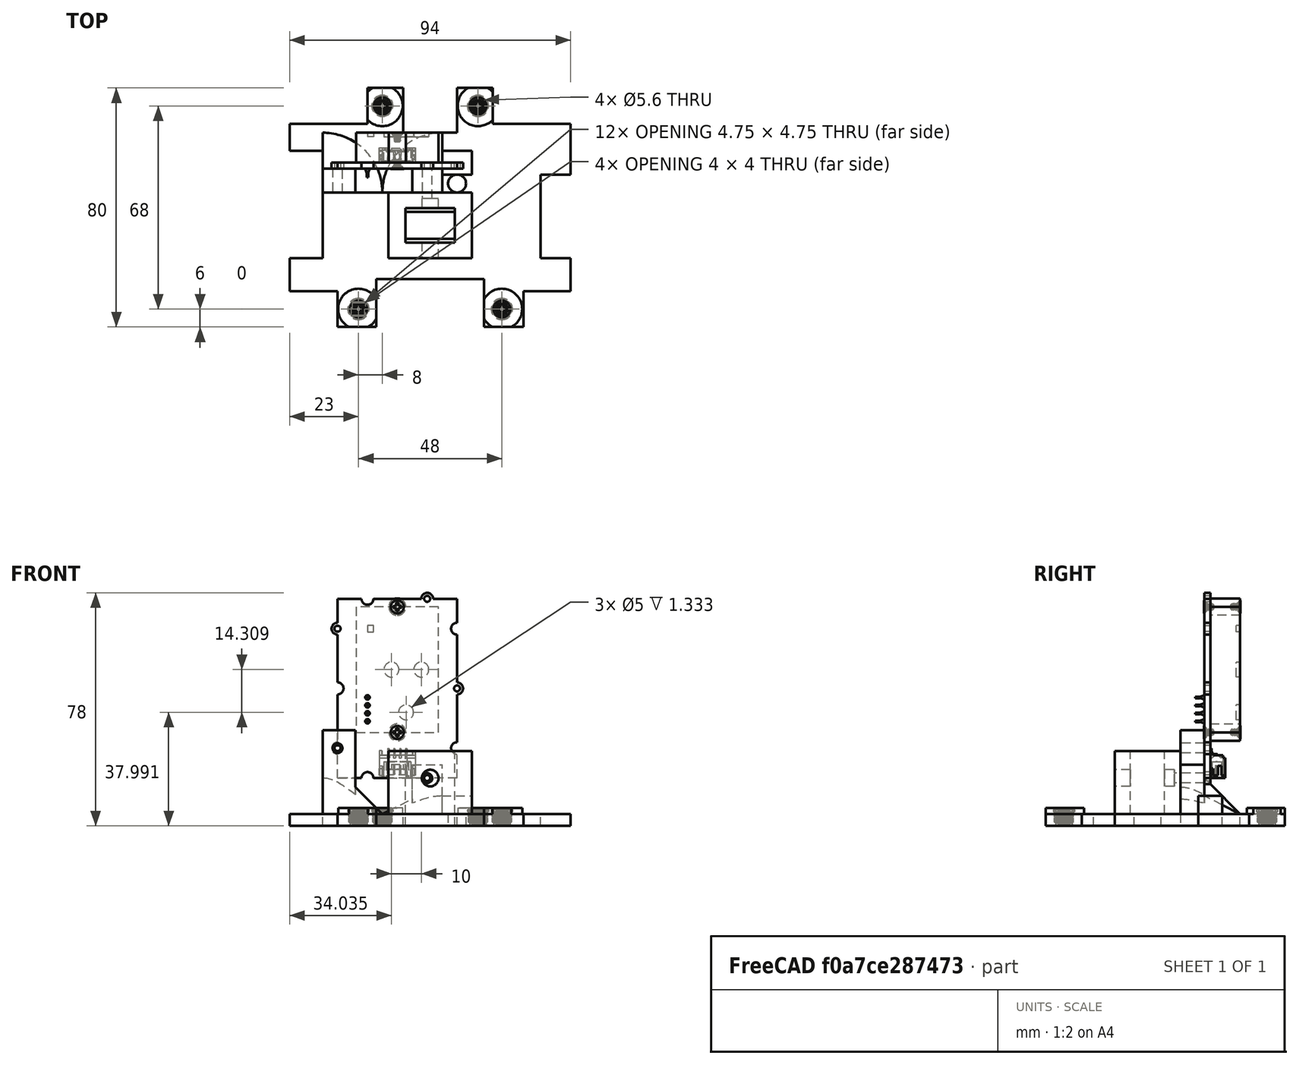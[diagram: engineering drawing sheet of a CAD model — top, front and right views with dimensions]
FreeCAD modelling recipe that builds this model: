
FCSTD DOCUMENT  (FreeCAD 0.20R29410 (Git))
Label: spine_11_06_2022
License: All rights reserved
LicenseURL: http://en.wikipedia.org/wiki/All_rights_reserved
objects: Part::Box×25, Part::Cylinder×18, Part::MultiFuse×16, Part::Cut×5, Part::Feature×5, Part::Cone×2
note: 71 computed .brp shape members not serialized (recipe doc carries the construction recipe); baked Part::Feature solids carry a one-line shape summary decoded from their .brp

FEATURE [Part::Cylinder] Cylinder103  label="Cylinder107"
  Angle = 360
  AttacherType = Attacher::AttachEngine3D
  FirstAngle = 0
  Height = 10
  Placement = pos=(63,3,0) rot=(0,0,1;0rad)
  Radius = 2.25
  SecondAngle = 0
FEATURE [Part::Box] Box064  label="base005"
  AttacherType = Attacher::AttachEngine3D
  Height = 4
  Length = 26
  Placement = pos=(-10.25,68,0) rot=(0,0,1;0rad)
  Width = 12
FEATURE [Part::Box] Box060  label="base001"
  AttacherType = Attacher::AttachEngine3D
  Height = 4
  Length = 94
  Width = 80
FEATURE [Part::Box] Box061  label="base002"
  AttacherType = Attacher::AttachEngine3D
  Height = 4
  Length = 26
  Width = 12
FEATURE [Part::Box] Box062  label="base003"
  AttacherType = Attacher::AttachEngine3D
  Height = 4
  Length = 26
  Placement = pos=(68,0,0) rot=(0,0,1;0rad)
  Width = 12
FEATURE [Part::Cylinder] Cylinder104  label="Cylinder103"
  Angle = 360
  AttacherType = Attacher::AttachEngine3D
  FirstAngle = 0
  Height = 10
  Placement = pos=(71,71,0) rot=(0,0,1;0rad)
  Radius = 2.25
  SecondAngle = 0
FEATURE [Part::Cylinder] Cylinder106  label="Cylinder104"
  Angle = 360
  AttacherType = Attacher::AttachEngine3D
  FirstAngle = 0
  Height = 10
  Placement = pos=(23,71,0) rot=(0,0,1;0rad)
  Radius = 2
  SecondAngle = 0
FEATURE [Part::Cylinder] Cylinder105  label="Cylinder108"
  Angle = 360
  AttacherType = Attacher::AttachEngine3D
  FirstAngle = 0
  Height = 10
  Placement = pos=(31,3,0) rot=(0,0,1;0rad)
  Radius = 2.25
  SecondAngle = 0
FEATURE [Part::Box] Box081  label="Cube039"
  AttacherType = Attacher::AttachEngine3D
  Height = 10
  Length = 10
  Placement = pos=(111.92,27,140) rot=(0,0,1;0rad)
  Width = 36
FEATURE [Part::Box] Box082  label="Cube040"
  AttacherType = Attacher::AttachEngine3D
  Height = 10
  Length = 36
  Placement = pos=(42,1,140) rot=(0,0,1;0rad)
  Width = 19
FEATURE [Part::Box] Box073  label="baseSpineCut"
  AttacherType = Attacher::AttachEngine3D
  Height = 25
  Length = 16.5
  Placement = pos=(51.75,33.5,140) rot=(0,0,1;0rad)
  Width = 9
FEATURE [Part::Cylinder] Cylinder107  label="Cylinder109"
  Angle = 360
  AttacherType = Attacher::AttachEngine3D
  FirstAngle = 0
  Height = 10
  Radius = 1
  SecondAngle = 0
FEATURE [Part::MultiFuse] Fusion123  label="screwIns001"
  Placement = pos=(0,3,0) rot=(0,0,1;0rad)
  Shapes = -> [Cylinder105,Cylinder107,Cylinder103,Cylinder104,Cylinder106]
FEATURE [Part::Box] Box080  label="Cube038"
  AttacherType = Attacher::AttachEngine3D
  Height = 10
  Length = 22
  Placement = pos=(2,27,140) rot=(0,0,1;0rad)
  Width = 22
FEATURE [Part::Box] Box063  label="base004"
  AttacherType = Attacher::AttachEngine3D
  Height = 4
  Length = 26
  Placement = pos=(78,68,0) rot=(0,0,1;0rad)
  Width = 12
FEATURE [Part::MultiFuse] Fusion122
  Shapes = -> [Box064,Box063,Box061,Box062]
FEATURE [Part::Cut] Cut019  label="baseNew"
  Base = -> Box060
  Tool = -> Fusion122
FEATURE [Part::Cut] Cut020  label="baseNew001"
  Base = -> Cut019
  Placement = pos=(107,84,140) rot=(0,0,1;3.14159rad)
  Tool = -> Fusion123
FEATURE [Part::Box] Box083  label="outerCut"
  AttacherType = Attacher::AttachEngine3D
  Height = 25
  Length = 16.5
  Placement = pos=(51.75,32.25,144) rot=(0,0,1;0rad)
  Width = 11.5
FEATURE [Part::Box] Box084  label="Cube042"
  AttacherType = Attacher::AttachEngine3D
  Height = 51
  Length = 50
  Placement = pos=(24,49,140) rot=(0,0,1;0rad)
  Width = 8
FEATURE [Part::Box] Box085  label="Cube043"
  AttacherType = Attacher::AttachEngine3D
  Height = 10
  Length = 15
  Placement = pos=(69,69,140) rot=(0,0,1;1.5708rad)
  Width = 18
FEATURE [Part::Box] Box086  label="baseSpineIn"
  AttacherType = Attacher::AttachEngine3D
  Height = 25
  Length = 28
  Placement = pos=(46,27,140) rot=(0,0,1;0rad)
  Width = 22
FEATURE [Part::Cylinder] Cylinder
  Angle = 360
  AttacherType = Attacher::AttachEngine3D
  FirstAngle = 0
  Height = 50
  Placement = pos=(60,-3,156) rot=(-1,0,0;1.5708rad)
  Radius = 2.8
  SecondAngle = 0
FEATURE [Part::Feature] Feature  label="Seed Grove SCD30"
  Placement = pos=(29,59,156) rot=(0.707107,0,0.707107;3.14159rad)
  shape: bbox 44 x 15.1 x 64 mm, 422 faces, 13 solids (baked)
FEATURE [Part::Cylinder] Cylinder108  label="Cylinder110"
  Angle = 360
  AttacherType = Attacher::AttachEngine3D
  FirstAngle = 0
  Height = 50
  Placement = pos=(80,17,186) rot=(-1,0,0;1.5708rad)
  Radius = 1.65
  SecondAngle = 0
FEATURE [Part::Cylinder] Cylinder109  label="Cylinder111"
  Angle = 360
  AttacherType = Attacher::AttachEngine3D
  FirstAngle = 0
  Height = 50
  Placement = pos=(40,17,166) rot=(-1,0,0;1.5708rad)
  Radius = 1.65
  SecondAngle = 0
FEATURE [Part::Cylinder] Cylinder110  label="Cylinder112"
  Angle = 360
  AttacherType = Attacher::AttachEngine3D
  FirstAngle = 0
  Height = 50
  Placement = pos=(70,17,156) rot=(-1,0,0;1.5708rad)
  Radius = 1.65
  SecondAngle = 0
FEATURE [Part::MultiFuse] Fusion  label="m2Cuts"
  Placement = pos=(-11,30,0) rot=(0,0,1;0rad)
  Shapes = -> [Cylinder108,Cylinder109,Cylinder110]
FEATURE [Part::Box] Box087  label="Cube044"
  AttacherType = Attacher::AttachEngine3D
  Height = 51
  Length = 50
  Placement = pos=(13,49,172) rot=(0,0,1;0rad)
  Width = 8
FEATURE [Part::Box] Box088  label="Cube045"
  AttacherType = Attacher::AttachEngine3D
  Height = 51
  Length = 19
  Placement = pos=(35,49,144) rot=(0,0,1;0rad)
  Width = 8
FEATURE [Part::MultiFuse] Fusion124  label="base"
  Shapes = -> [Cut020,Box084,Box086]
FEATURE [Part::MultiFuse] Fusion125  label="cuts"
  Shapes = -> [Box087,Box088,Fusion,Box085,Box080,Box083,Box082,Box081,Box073,Cylinder]
FEATURE [Part::Box] Box089  label="Cube046"
  AttacherType = Attacher::AttachEngine3D
  Height = 10
  Length = 11
  Placement = pos=(13,57,140) rot=(0,0,1;0rad)
  Width = 6
FEATURE [Part::Feature] Solid  label="m4HeatSet"
  Placement = pos=(36,10,140) rot=(1,0,0;1.5708rad)
  shape: bbox 7.1 x 7.1 x 6.065 mm, 234 faces (baked)
FEATURE [Part::Feature] Solid001  label="m4HeatSet001"
  Placement = pos=(84,10,140) rot=(1,0,0;1.5708rad)
  shape: bbox 7.1 x 7.1 x 6.065 mm, 234 faces (baked)
FEATURE [Part::Feature] Solid002  label="m4HeatSet002"
  Placement = pos=(44,78,140) rot=(1,0,0;1.5708rad)
  shape: bbox 7.1 x 7.1 x 6.065 mm, 234 faces (baked)
FEATURE [Part::Feature] Solid003  label="m4HeatSet003"
  Placement = pos=(76,78,140) rot=(1,0,0;1.5708rad)
  shape: bbox 7.1 x 7.1 x 6.065 mm, 234 faces (baked)
FEATURE [Part::Cylinder] Cylinder111  label="m4HeatSetCut"
  Angle = 360
  AttacherType = Attacher::AttachEngine3D
  FirstAngle = 0
  Height = 10
  Placement = pos=(36,10,140) rot=(0,0,1;0rad)
  Radius = 2.8
  SecondAngle = 0
FEATURE [Part::Cylinder] Cylinder112  label="m4HeatSetCut001"
  Angle = 360
  AttacherType = Attacher::AttachEngine3D
  FirstAngle = 0
  Height = 10
  Placement = pos=(84,10,140) rot=(0,0,1;0rad)
  Radius = 2.8
  SecondAngle = 0
FEATURE [Part::Cylinder] Cylinder113  label="m4HeatSetCut002"
  Angle = 360
  AttacherType = Attacher::AttachEngine3D
  FirstAngle = 0
  Height = 10
  Placement = pos=(76,78,140) rot=(0,0,1;0rad)
  Radius = 2.8
  SecondAngle = 0
FEATURE [Part::Cylinder] Cylinder114  label="m4HeatSetCut003"
  Angle = 360
  AttacherType = Attacher::AttachEngine3D
  FirstAngle = 0
  Height = 10
  Placement = pos=(44,78,140) rot=(0,0,1;0rad)
  Radius = 2.8
  SecondAngle = 0
FEATURE [Part::MultiFuse] Fusion126  label="heatSetCuts"
  Shapes = -> [Cylinder111,Cylinder112,Cylinder113,Cylinder114]
FEATURE [Part::Box] Box091  label="Cube048"
  AttacherType = Attacher::AttachEngine3D
  Height = 10
  Length = 11
  Placement = pos=(13,49,140) rot=(0,0,1;0rad)
  Width = 8
FEATURE [Part::MultiFuse] Fusion127  label="cuts001"
  Shapes = -> [Box091,Fusion126,Box089,Fusion125]
FEATURE [Part::Cylinder] Cylinder115  label="m4HeatSetCut004"
  Angle = 360
  AttacherType = Attacher::AttachEngine3D
  FirstAngle = 0
  Height = 6
  Placement = pos=(36,10,140) rot=(0,0,-1;1.0472rad)
  Radius = 6.8
  SecondAngle = 0
FEATURE [Part::Cylinder] Cylinder116  label="m4HeatSetCut005"
  Angle = 360
  AttacherType = Attacher::AttachEngine3D
  FirstAngle = 0
  Height = 6
  Placement = pos=(84,10,140) rot=(0,0,1;0rad)
  Radius = 6.8
  SecondAngle = 0
FEATURE [Part::Cylinder] Cylinder117  label="m4HeatSetCut006"
  Angle = 360
  AttacherType = Attacher::AttachEngine3D
  FirstAngle = 0
  Height = 6
  Placement = pos=(76,78,140) rot=(0,0,1;0rad)
  Radius = 6.8
  SecondAngle = 0
FEATURE [Part::Cylinder] Cylinder118  label="m4HeatSetCut007"
  Angle = 360
  AttacherType = Attacher::AttachEngine3D
  FirstAngle = 0
  Height = 6
  Placement = pos=(44,78,140) rot=(0,0,1;0rad)
  Radius = 6.8
  SecondAngle = 0
FEATURE [Part::MultiFuse] Fusion128  label="heatSetAddOns"
  Shapes = -> [Cylinder115,Cylinder116,Cylinder117,Cylinder118]
FEATURE [Part::Box] Box092  label="Cube049"
  AttacherType = Attacher::AttachEngine3D
  Height = 10
  Length = 94
  Placement = pos=(13,-4,140) rot=(0,0,1;0rad)
  Width = 8
FEATURE [Part::MultiFuse] Fusion129  label="base006"
  Shapes = -> [Fusion128,Fusion124]
FEATURE [Part::Box] Box093  label="Cube050"
  AttacherType = Attacher::AttachEngine3D
  Height = 10
  Length = 94
  Placement = pos=(13,84,140) rot=(0,0,1;0rad)
  Width = 8
FEATURE [Part::Box] Box094  label="Cube051"
  AttacherType = Attacher::AttachEngine3D
  Height = 10
  Length = 94
  Placement = pos=(89,72,140) rot=(0,0,1;1.5708rad)
  Width = 8
FEATURE [Part::Box] Box095  label="Cube052"
  AttacherType = Attacher::AttachEngine3D
  Height = 10
  Length = 94
  Placement = pos=(39,72,140) rot=(0,0,1;1.5708rad)
  Width = 8
FEATURE [Part::MultiFuse] Fusion130
  Shapes = -> [Box093,Box094,Box095,Box092]
FEATURE [Part::MultiFuse] Fusion131  label="cuts002"
  Shapes = -> [Fusion127,Fusion130]
FEATURE [Part::Box] Box096  label="Cube053"
  AttacherType = Attacher::AttachEngine3D
  Height = 10
  Length = 10
  Placement = pos=(97,27,140) rot=(0,0,1;0rad)
  Width = 28
FEATURE [Part::MultiFuse] Fusion132  label="cuts003"
  Shapes = -> [Fusion131,Box096]
FEATURE [Part::Cut] Cut  label="base007"
  Base = -> Fusion129
  Tool = -> Fusion132
FEATURE [Part::Cone] Cone
  Angle = 90
  AttacherType = Attacher::AttachEngine3D
  Height = 12
  Placement = pos=(24,49,144) rot=(0,0,1;0rad)
  Radius1 = 20
  Radius2 = 8
FEATURE [Part::Box] Box  label="Cube"
  AttacherType = Attacher::AttachEngine3D
  Height = 60
  Length = 11
  Placement = pos=(64,49,144) rot=(0,0,1;0rad)
  Width = 8
FEATURE [Part::Box] Box097  label="Cube054"
  AttacherType = Attacher::AttachEngine3D
  Height = 55
  Length = 11
  Placement = pos=(54,49,160.5) rot=(0,0,1;0rad)
  Width = 8
FEATURE [Part::MultiFuse] Fusion133  label="cuts004"
  Shapes = -> [Box,Box097]
FEATURE [Part::Cut] Cut021
  Base = -> Cut
  Tool = -> Fusion133
FEATURE [Part::Cylinder] Cylinder119  label="m4HeatSetCut008"
  Angle = 360
  AttacherType = Attacher::AttachEngine3D
  FirstAngle = 0
  Height = 10
  Placement = pos=(69,52,140) rot=(0,0,1;0rad)
  Radius = 3
  SecondAngle = 0
FEATURE [Part::MultiFuse] Fusion134
  Shapes = -> [Cone,Cut021]
FEATURE [Part::Cut] Cut022
  Base = -> Fusion134
  Tool = -> Cylinder119
FEATURE [Part::Box] Box098  label="Cube055"
  AttacherType = Attacher::AttachEngine3D
  Height = 10
  Length = 10
  Placement = pos=(64,55,140) rot=(0,0,1;0rad)
  Width = 8
FEATURE [Part::MultiFuse] Fusion135
  Shapes = -> [Cut022,Box098]
FEATURE [Part::Cone] Cone001
  Angle = 90
  AttacherType = Attacher::AttachEngine3D
  Height = 6
  Placement = pos=(64,49,144) rot=(0,0,1;1.5708rad)
  Radius1 = 20
  Radius2 = 8
FEATURE [Part::MultiFuse] Fusion136
  Shapes = -> [Fusion135,Cone001]
